# Revit family: Plumbing_Drainage_Zurn_Z1750_Sani-Flor-Receptor
name_source: partatom
category: Plumbing Fixtures
units: mm (PartAtom-declared; Revit-internal decimal feet)

## family parameters
Always vertical = Yes
Cut with Voids When Loaded = No
Maintain Annotation Orientation = No
OmniClass Number = 23.45.05.14.14
OmniClass Title = Sinks/Lavatories
Part Type = Normal
Room Calculation Point = No
Round Connector Dimension = Use Radius
Shared = No
Work Plane-Based = No

## types (16) — shared parameters
Assembly Code = D2030300
CW Connection = No
Default Elevation = 2 "
Description = 12 X 12 [305 x 305] SANI-FLOR RECEPTOR 6 [152] SUMP DEPTH
HW Connection = No
Manufacturer = Zurn Water, LLC
Manufacurer Brand = Zurn
Model = Z1750
Modified Date = 06/25/25
Product Documentation Link = https://files.zurn.com
Product Page URL = https://www.zurn.com
Product data url = https://www.bimobject.com
Sink Sump Depth = 6 "
URL = www.zurn.com
Vent Connection = No
Waste Connection = Yes
Width = 12 "
zero-valued in all types: CWFU, HWFU, WFU

## per-type parameters (varying)
| type | Actual Pipe Size Outer Diameter (A) | Approx. Weight (Lbs) | Body Height (E) | Main Material | Nominal Pipe Size (A) | Outlet Connection | Outlet Inner Radius | Type Comments |
| Z1750 - 3" - IC Outlet | 3.5 " | 15 " | 8.563 " | Steel - Zurn - Stainless 304 | 3 " | 1.5 " | 1.75 " | Z1750 Sani-Flor receptor - 3" IC Outlet |
| Z1750 - 4" - IC Outlet | 4.5 " | 15 " | 8.563 " | Steel - Zurn - Stainless 304 | 4 " | 2 " | 2.25 " | Z1750 Sani-Flor receptor - 4" IC Outlet |
| Z1750 - 2"- NH Outlet | 2.375 " | 15 " | 8.063 " | Steel - Zurn - Stainless 304 | 2 " | 1 " | 1.188 " | Z1750 Sani-Flor receptor - 2" NH Outlet |
| Z1750 - 3" - NH Outlet | 3.5 " | 15 " | 8.063 " | Steel - Zurn - Stainless 304 | 3 " | 1.5 " | 1.75 " | Z1750 Sani-Flor receptor - 3" NH Outlet |
| Z1750 - 4" - NH Outlet | 4.5 " | 15 " | 8.063 " | Steel - Zurn - Stainless 304 | 4 " | 2 " | 2.25 " | Z1750 Sani-Flor receptor - 4" NH Outlet |
| Z1750 - 6" - NH Outlet | 6.625 " | 17 " | 8.063 " | Steel - Zurn - Stainless 304 | 6 " | 3 " | 3.313 " | Z1750 Sani-Flor receptor - 6" NH Outlet |
| Z1750 - 3" - NL Outlet | 3.5 " | 15 " | 7.813 " | Steel - Zurn - Stainless 304 | 3 " | 1.5 " | 1.75 " | Z1750 Sani-Flor receptor - 3" NL Outlet |
| Z1750 - 4" - NL Outlet | 4.5 " | 15 " | 7.813 " | Steel - Zurn - Stainless 304 | 4 " | 2 " | 2.25 " | Z1750 Sani-Flor receptor - 4" NL Outlet |
| ZM1750 - 3" - IC Outlet | 3.5 " | 15 " | 8.563 " | Steel - Zurn - Stainless 316 | 3 " | 1.5 " | 1.75 " | ZM1750 Sani-Flor receptor - 3" IC Outlet |
| ZM1750 - 4" - IC Outlet | 4.5 " | 15 " | 8.563 " | Steel - Zurn - Stainless 316 | 4 " | 2 " | 2.25 " | ZM1750 Sani-Flor receptor - 4" IC Outlet |
| ZM1750 - 2"- NH Outlet | 2.375 " | 15 " | 8.063 " | Steel - Zurn - Stainless 316 | 2 " | 1 " | 1.188 " | ZM1750 Sani-Flor receptor - 2" NH Outlet |
| ZM1750 - 3" - NH Outlet | 3.5 " | 15 " | 8.063 " | Steel - Zurn - Stainless 316 | 3 " | 1.5 " | 1.75 " | ZM1750 Sani-Flor receptor - 3" NH Outlet |
| ZM1750 - 4" - NH Outlet | 4.5 " | 15 " | 8.063 " | Steel - Zurn - Stainless 316 | 4 " | 2 " | 2.25 " | ZM1750 Sani-Flor receptor - 4" NH Outlet |
| ZM1750 - 6" - NH Outlet | 6.625 " | 17 " | 8.063 " | Steel - Zurn - Stainless 316 | 6 " | 3 " | 3.313 " | ZM1750 Sani-Flor receptor - 6" NH Outlet |
| ZM1750 - 3" - NL Outlet | 3.5 " | 15 " | 7.813 " | Steel - Zurn - Stainless 316 | 3 " | 1.5 " | 1.75 " | ZM1750 Sani-Flor receptor - 3" NL Outlet |
| ZM1750 - 4" - NL Outlet | 4.5 " | 15 " | 7.813 " | Steel - Zurn - Stainless 316 | 4 " | 2 " | 2.25 " | ZM1750 Sani-Flor receptor - 4" NL Outlet |

## geometry (parser evidence)
native form markers: Sweep x2
no freeform markers — native parametric forms only
